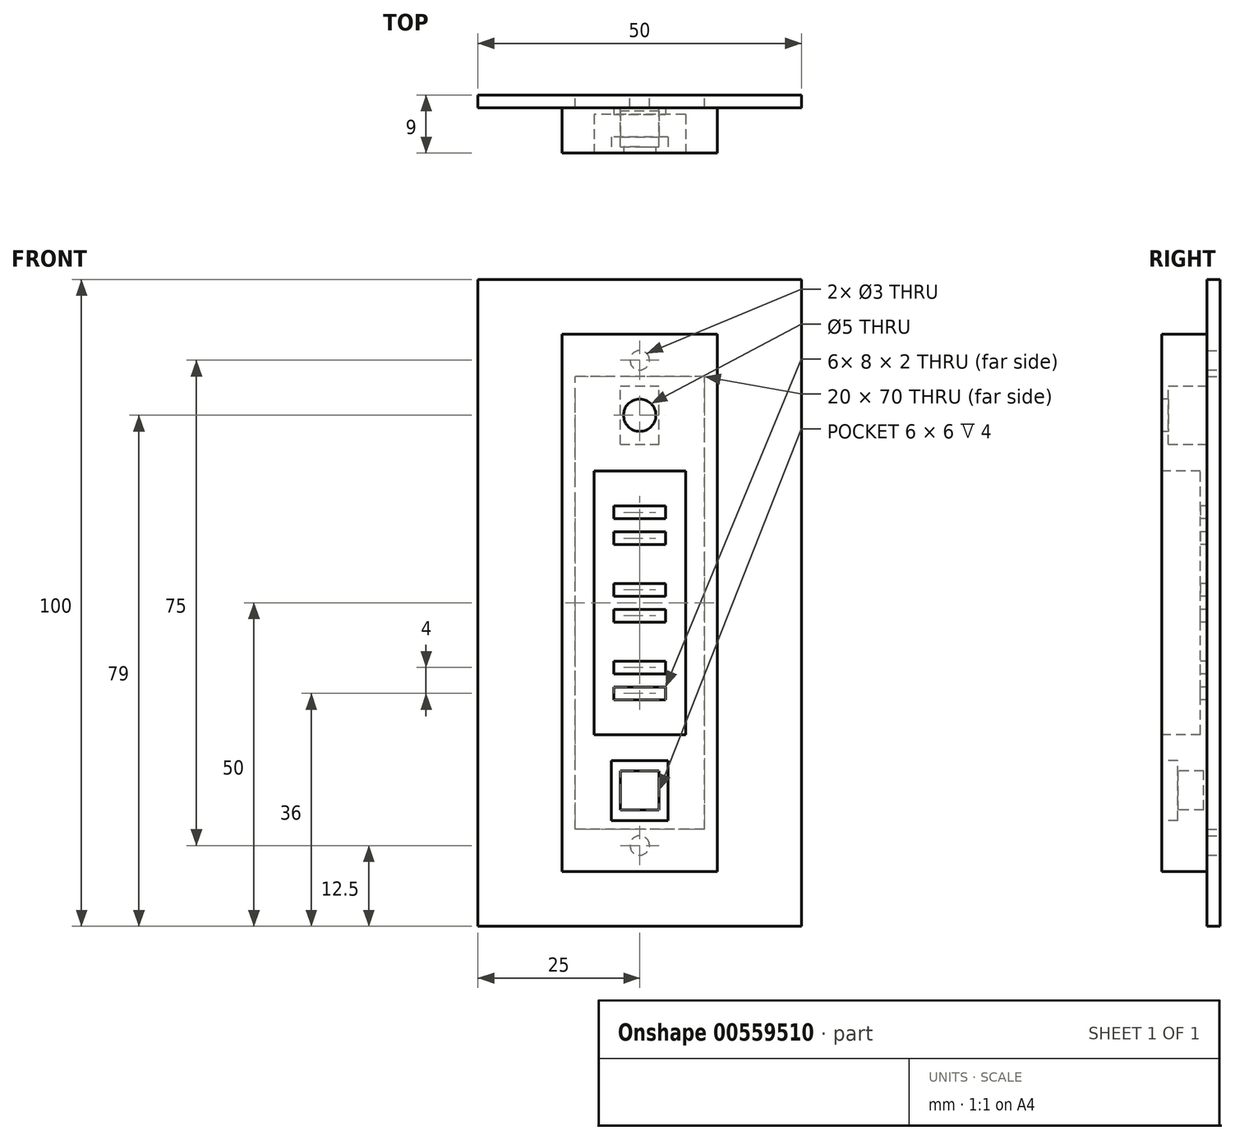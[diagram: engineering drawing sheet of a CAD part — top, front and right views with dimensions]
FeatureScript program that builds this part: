
annotation { "Feature Type Name" : "Feature", "Feature Type Description" : "" }
export const myFeature = defineFeature(function(context is Context, id is Id, definition is map)
    precondition{}
    {
        {
            var Q0;
            Q0=qCreatedBy(makeId("Front.planeOp"),FACE);
            var sketch = newSketch(context, id + "F0", { "sketchPlane" : qUnion([Q0])});
            skLineSegment(sketch, "E0.bottom", {"start": v(25, -50) * mm, "end": v(-25, -50) * mm});
            skLineSegment(sketch, "E0.top", {"start": v(25, 50) * mm, "end": v(-25, 50) * mm});
            skLineSegment(sketch, "E0.left", {"start": v(25, -50) * mm, "end": v(25, 50) * mm});
            skLineSegment(sketch, "E0.right", {"start": v(-25, -50) * mm, "end": v(-25, 50) * mm});
            skPoint(sketch, "E0.middle", {"position": v(0, 0) * mm});
            skLineSegment(sketch, "E1.bottom", {"start": v(10, -35) * mm, "end": v(-10, -35) * mm});
            skLineSegment(sketch, "E1.top", {"start": v(10, 35) * mm, "end": v(-10, 35) * mm});
            skLineSegment(sketch, "E1.left", {"start": v(10, -35) * mm, "end": v(10, 35) * mm});
            skLineSegment(sketch, "E1.right", {"start": v(-10, -35) * mm, "end": v(-10, 35) * mm});
            skCircle(sketch, "E2", {"center": v(0, 37.5) * mm, "radius": 1.5 * mm});
            skCircle(sketch, "E3", {"center": v(0, -37.5) * mm, "radius": 1.5 * mm});
            skSolve(sketch);
        }
        {
            var Q0;
            Q0=qSketchRegion(id+"F0",true);
            extrude(context, id + "F1", {"entities" : qUnion([Q0]), "depth" : 2 * mm});
        }
        {
            var Q0;
            Q0=makeQuery(id+"F1.opExtrude","CAP_FACE",FACE,{"disambiguationData":[OSD([sQuery(id+"F0.wireOp",EDGE,"E0.bottom"),sQuery(id+"F0.wireOp",EDGE,"E0.top"),sQuery(id+"F0.wireOp",EDGE,"E0.left"),sQuery(id+"F0.wireOp",EDGE,"E0.right"),sQuery(id+"F0.wireOp",EDGE,"E1.bottom"),sQuery(id+"F0.wireOp",EDGE,"E1.top"),sQuery(id+"F0.wireOp",EDGE,"E1.left"),sQuery(id+"F0.wireOp",EDGE,"E1.right"),sQuery(id+"F0.wireOp",EDGE,"E2"),sQuery(id+"F0.wireOp",EDGE,"E3")])],"isStart":false});
            cPlane(context, id + "F2", {"entities" : qUnion([Q0]), "cplaneType" : CPlaneType.OFFSET, "offset" : 0 * mm, "width" : 150 * mm, "height" : 150 * mm});
        }
        {
            var Q0;
            Q0=qCreatedBy(id+"F2.planeOp",FACE);
            var sketch = newSketch(context, id + "F3", { "sketchPlane" : qUnion([Q0])});
            skLineSegment(sketch, "E4.bottom", {"start": v(12, -41.5) * mm, "end": v(-12, -41.5) * mm});
            skLineSegment(sketch, "E4.top", {"start": v(12, 41.5) * mm, "end": v(-12, 41.5) * mm});
            skLineSegment(sketch, "E4.left", {"start": v(12, -41.5) * mm, "end": v(12, 41.5) * mm});
            skLineSegment(sketch, "E4.right", {"start": v(-12, -41.5) * mm, "end": v(-12, 41.5) * mm});
            skPoint(sketch, "E4.middle", {"position": v(0, 0) * mm});
            skSolve(sketch);
        }
        {
            var Q0;
            Q0=qSketchRegion(id+"F3",true);
            extrude(context, id + "F4", {"entities" : qUnion([Q0]), "depth" : 7 * mm});
        }
        {
            var Q0;
            Q0=makeQuery(id+"F4.opExtrude","CAP_FACE",FACE,{"disambiguationData":[OSD([sQuery(id+"F3.wireOp",EDGE,"E4.bottom"),sQuery(id+"F3.wireOp",EDGE,"E4.top"),sQuery(id+"F3.wireOp",EDGE,"E4.left"),sQuery(id+"F3.wireOp",EDGE,"E4.right")])],"isStart":false});
            var sketch = newSketch(context, id + "F5", { "sketchPlane" : qUnion([Q0])});
            skCircle(sketch, "E5", {"center": v(0, 29) * mm, "radius": 2.5 * mm});
            skLineSegment(sketch, "E6.bottom", {"start": v(2.5, 25) * mm, "end": v(-2.5, 25) * mm, "construction": true});
            skLineSegment(sketch, "E6.top", {"start": v(2.5, 33) * mm, "end": v(-2.5, 33) * mm, "construction": true});
            skLineSegment(sketch, "E6.left", {"start": v(2.5, 25) * mm, "end": v(2.5, 33) * mm, "construction": true});
            skLineSegment(sketch, "E6.right", {"start": v(-2.5, 25) * mm, "end": v(-2.5, 33) * mm, "construction": true});
            skCircle(sketch, "E7", {"center": v(-7.5, 32.5) * mm, "radius": 1 * mm, "construction": true});
            skCircle(sketch, "E8", {"center": v(7.5, 32.5) * mm, "radius": 1 * mm, "construction": true});
            skCircle(sketch, "E9", {"center": v(-7.5, -32.5) * mm, "radius": 1 * mm, "construction": true});
            skCircle(sketch, "E10", {"center": v(7.5, -32.5) * mm, "radius": 1 * mm, "construction": true});
            skSolve(sketch);
        }
        {
            var Q0;
            Q0=qSketchRegion(id+"F5",true);
            extrude(context, id + "F6", {"entities" : qUnion([Q0]), "operationType" : NewBodyOperationType.REMOVE, "oppositeDirection" : true, "depth" : 5 * mm});
        }
        {
            var Q0;
            Q0=makeQuery(id+"F4.opExtrude","CAP_FACE",FACE,{"disambiguationData":[OSD([sQuery(id+"F3.wireOp",EDGE,"E4.bottom"),sQuery(id+"F3.wireOp",EDGE,"E4.top"),sQuery(id+"F3.wireOp",EDGE,"E4.left"),sQuery(id+"F3.wireOp",EDGE,"E4.right")])],"isStart":true});
            var sketch = newSketch(context, id + "F7", { "sketchPlane" : qUnion([Q0])});
            skLineSegment(sketch, "E11.bottom", {"start": v(3, 24.5) * mm, "end": v(-3, 24.5) * mm});
            skLineSegment(sketch, "E11.top", {"start": v(3, 33.5) * mm, "end": v(-3, 33.5) * mm});
            skLineSegment(sketch, "E11.left", {"start": v(3, 24.5) * mm, "end": v(3, 33.5) * mm});
            skLineSegment(sketch, "E11.right", {"start": v(-3, 24.5) * mm, "end": v(-3, 33.5) * mm});
            skPoint(sketch, "E11.middle", {"position": v(0, 29) * mm});
            skSolve(sketch);
        }
        {
            var Q0;
            Q0=qSketchRegion(id+"F7",true);
            extrude(context, id + "F8", {"entities" : qUnion([Q0]), "operationType" : NewBodyOperationType.REMOVE, "oppositeDirection" : true, "depth" : 6 * mm});
        }
        {
            var Q0;
            Q0=makeQuery(id+"F4.opExtrude","CAP_FACE",FACE,{"disambiguationData":[OSD([sQuery(id+"F3.wireOp",EDGE,"E4.bottom"),sQuery(id+"F3.wireOp",EDGE,"E4.top"),sQuery(id+"F3.wireOp",EDGE,"E4.left"),sQuery(id+"F3.wireOp",EDGE,"E4.right")])],"isStart":false});
            var sketch = newSketch(context, id + "F9", { "sketchPlane" : qUnion([Q0])});
            skLineSegment(sketch, "E12.bottom", {"start": v(4, 13) * mm, "end": v(-4, 13) * mm});
            skLineSegment(sketch, "E12.top", {"start": v(4, 15) * mm, "end": v(-4, 15) * mm});
            skLineSegment(sketch, "E12.left", {"start": v(4, 13) * mm, "end": v(4, 15) * mm});
            skLineSegment(sketch, "E12.right", {"start": v(-4, 13) * mm, "end": v(-4, 15) * mm});
            skPoint(sketch, "E12.middle", {"position": v(0, 14) * mm});
            skLineSegment(sketch, "E13.bottom", {"start": v(4, 9) * mm, "end": v(-4, 9) * mm});
            skLineSegment(sketch, "E13.top", {"start": v(4, 11) * mm, "end": v(-4, 11) * mm});
            skLineSegment(sketch, "E13.left", {"start": v(4, 9) * mm, "end": v(4, 11) * mm});
            skLineSegment(sketch, "E13.right", {"start": v(-4, 9) * mm, "end": v(-4, 11) * mm});
            skPoint(sketch, "E13.middle", {"position": v(0, 10) * mm});
            skLineSegment(sketch, "E14.bottom", {"start": v(4, 1) * mm, "end": v(-4, 1) * mm});
            skLineSegment(sketch, "E14.top", {"start": v(4, 3) * mm, "end": v(-4, 3) * mm});
            skLineSegment(sketch, "E14.left", {"start": v(4, 1) * mm, "end": v(4, 3) * mm});
            skLineSegment(sketch, "E14.right", {"start": v(-4, 1) * mm, "end": v(-4, 3) * mm});
            skPoint(sketch, "E14.middle", {"position": v(0, 2) * mm});
            skLineSegment(sketch, "E15.bottom", {"start": v(4, -1) * mm, "end": v(-4, -1) * mm});
            skLineSegment(sketch, "E15.top", {"start": v(4, -3) * mm, "end": v(-4, -3) * mm});
            skLineSegment(sketch, "E15.left", {"start": v(4, -1) * mm, "end": v(4, -3) * mm});
            skLineSegment(sketch, "E15.right", {"start": v(-4, -1) * mm, "end": v(-4, -3) * mm});
            skPoint(sketch, "E15.middle", {"position": v(0, -2) * mm});
            skLineSegment(sketch, "E16.bottom", {"start": v(4, -9) * mm, "end": v(-4, -9) * mm});
            skLineSegment(sketch, "E16.top", {"start": v(4, -11) * mm, "end": v(-4, -11) * mm});
            skLineSegment(sketch, "E16.left", {"start": v(4, -9) * mm, "end": v(4, -11) * mm});
            skLineSegment(sketch, "E16.right", {"start": v(-4, -9) * mm, "end": v(-4, -11) * mm});
            skPoint(sketch, "E16.middle", {"position": v(0, -10) * mm});
            skPoint(sketch, "E16.middle.positionSnap0", {"position": v(0, -3) * mm});
            skPoint(sketch, "E16.centerSnap0", {"position": v(0, -3) * mm});
            skLineSegment(sketch, "E17.bottom", {"start": v(4, -13) * mm, "end": v(-4, -13) * mm});
            skLineSegment(sketch, "E17.top", {"start": v(4, -15) * mm, "end": v(-4, -15) * mm});
            skLineSegment(sketch, "E17.left", {"start": v(4, -13) * mm, "end": v(4, -15) * mm});
            skLineSegment(sketch, "E17.right", {"start": v(-4, -13) * mm, "end": v(-4, -15) * mm});
            skPoint(sketch, "E17.middle", {"position": v(0, -14) * mm});
            skSolve(sketch);
        }
        {
            var Q0;
            Q0=qSketchRegion(id+"F9",true);
            extrude(context, id + "F10", {"entities" : qUnion([Q0]), "operationType" : NewBodyOperationType.REMOVE, "oppositeDirection" : true, "depth" : 10 * mm});
        }
        {
            var Q0;
            Q0=makeQuery(id+"F4.opExtrude","CAP_FACE",FACE,{"disambiguationData":[OSD([sQuery(id+"F3.wireOp",EDGE,"E4.bottom"),sQuery(id+"F3.wireOp",EDGE,"E4.top"),sQuery(id+"F3.wireOp",EDGE,"E4.left"),sQuery(id+"F3.wireOp",EDGE,"E4.right")])],"isStart":false});
            var sketch = newSketch(context, id + "F11", { "sketchPlane" : qUnion([Q0])});
            skLineSegment(sketch, "E18.bottom", {"start": v(7.07, -20.36) * mm, "end": v(-7.07, -20.36) * mm});
            skLineSegment(sketch, "E18.top", {"start": v(7.07, 20.36) * mm, "end": v(-7.07, 20.36) * mm});
            skLineSegment(sketch, "E18.left", {"start": v(7.07, -20.36) * mm, "end": v(7.07, 20.36) * mm});
            skLineSegment(sketch, "E18.right", {"start": v(-7.07, -20.36) * mm, "end": v(-7.07, 20.36) * mm});
            skPoint(sketch, "E18.middle", {"position": v(0, 0) * mm});
            skSolve(sketch);
        }
        {
            var Q0;
            Q0=qSketchRegion(id+"F11",true);
            extrude(context, id + "F12", {"entities" : qUnion([Q0]), "operationType" : NewBodyOperationType.REMOVE, "oppositeDirection" : true, "depth" : 6 * mm});
        }
        {
            var Q0;
            Q0=makeQuery(id+"F4.opExtrude","CAP_FACE",FACE,{"disambiguationData":[OSD([sQuery(id+"F3.wireOp",EDGE,"E4.bottom"),sQuery(id+"F3.wireOp",EDGE,"E4.top"),sQuery(id+"F3.wireOp",EDGE,"E4.left"),sQuery(id+"F3.wireOp",EDGE,"E4.right")])],"isStart":false});
            var sketch = newSketch(context, id + "F13", { "sketchPlane" : qUnion([Q0])});
            skLineSegment(sketch, "E19.bottom", {"start": v(3, -32) * mm, "end": v(-3, -32) * mm});
            skLineSegment(sketch, "E19.top", {"start": v(3, -26) * mm, "end": v(-3, -26) * mm});
            skLineSegment(sketch, "E19.left", {"start": v(3, -32) * mm, "end": v(3, -26) * mm});
            skLineSegment(sketch, "E19.right", {"start": v(-3, -32) * mm, "end": v(-3, -26) * mm});
            skPoint(sketch, "E19.middle", {"position": v(0, -29) * mm});
            skSolve(sketch);
        }
        {
            var Q0;
            Q0=qSketchRegion(id+"F13",true);
            extrude(context, id + "F14", {"entities" : qUnion([Q0]), "operationType" : NewBodyOperationType.REMOVE, "oppositeDirection" : true, "depth" : 6.5 * mm});
        }
        {
            var Q0;
            Q0=makeQuery(id+"F4.opExtrude","CAP_FACE",FACE,{"disambiguationData":[OSD([sQuery(id+"F3.wireOp",EDGE,"E4.bottom"),sQuery(id+"F3.wireOp",EDGE,"E4.top"),sQuery(id+"F3.wireOp",EDGE,"E4.left"),sQuery(id+"F3.wireOp",EDGE,"E4.right")])],"isStart":false});
            var sketch = newSketch(context, id + "F15", { "sketchPlane" : qUnion([Q0])});
            skLineSegment(sketch, "E20.bottom", {"start": v(4.4, -33.62) * mm, "end": v(-4.4, -33.62) * mm});
            skLineSegment(sketch, "E20.top", {"start": v(4.4, -24.38) * mm, "end": v(-4.4, -24.38) * mm});
            skLineSegment(sketch, "E20.left", {"start": v(4.4, -33.62) * mm, "end": v(4.4, -24.38) * mm});
            skLineSegment(sketch, "E20.right", {"start": v(-4.4, -33.62) * mm, "end": v(-4.4, -24.38) * mm});
            skPoint(sketch, "E20.middle", {"position": v(0, -29) * mm});
            skPoint(sketch, "E20.middle.positionSnap0", {"position": v(0, -26) * mm});
            skPoint(sketch, "E20.middle.positionSnap1", {"position": v(3, -29) * mm});
            skPoint(sketch, "E20.centerSnap0", {"position": v(0, -26) * mm});
            skPoint(sketch, "E20.centerSnap1", {"position": v(3, -29) * mm});
            skSolve(sketch);
        }
        {
            var Q0;
            Q0=qSketchRegion(id+"F15",true);
            extrude(context, id + "F16", {"entities" : qUnion([Q0]), "operationType" : NewBodyOperationType.REMOVE, "oppositeDirection" : true, "depth" : 2.5 * mm});
        }
    });
